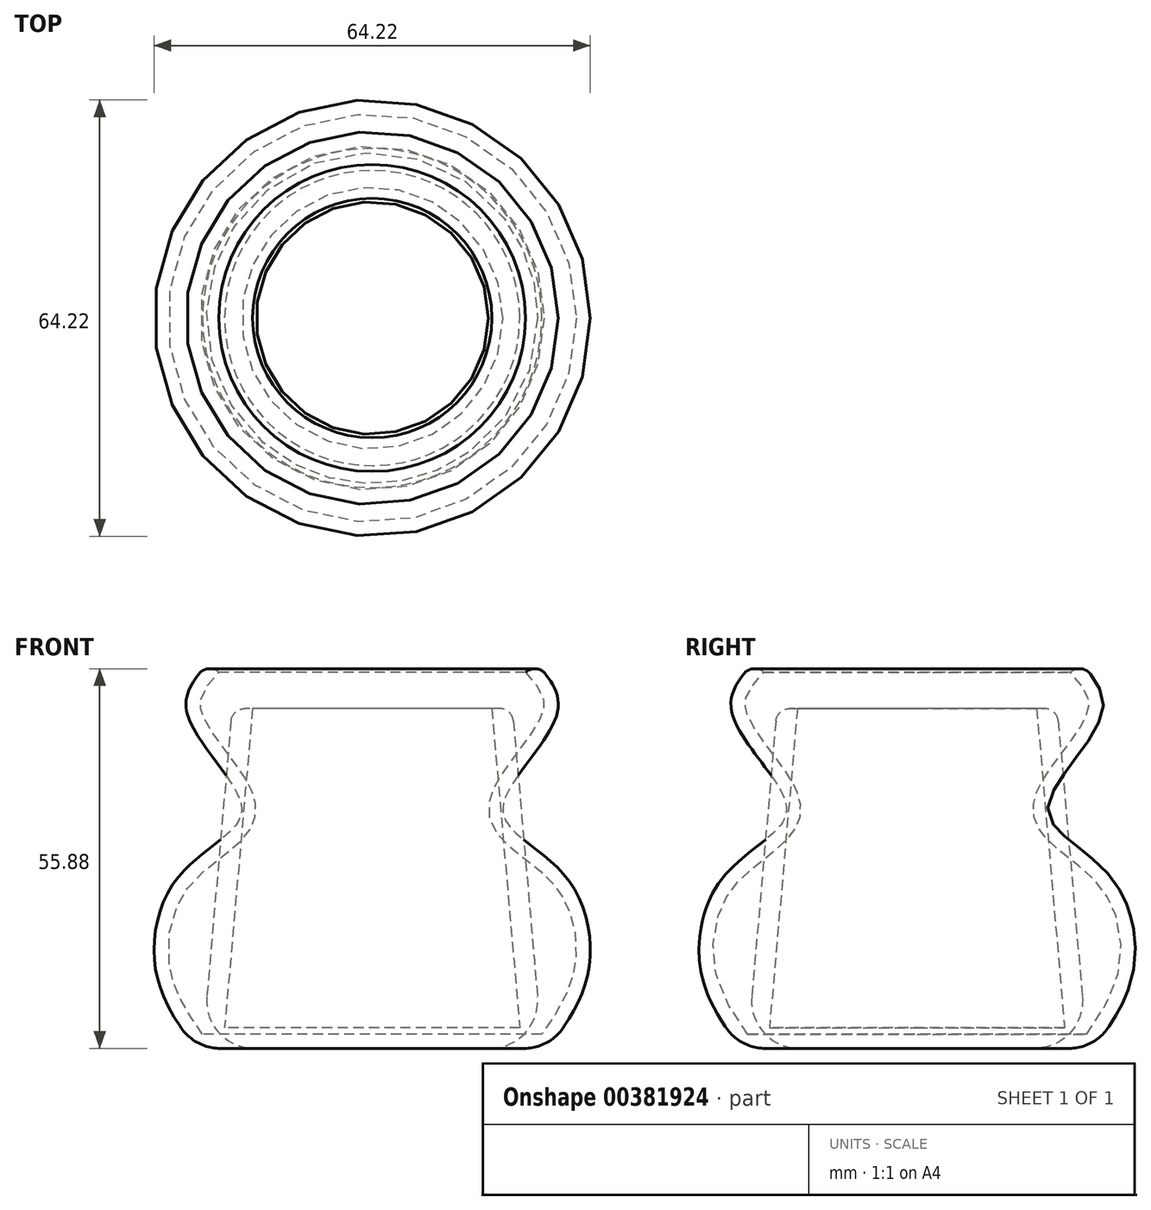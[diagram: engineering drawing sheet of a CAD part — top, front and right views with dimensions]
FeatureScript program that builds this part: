
annotation { "Feature Type Name" : "Feature", "Feature Type Description" : "" }
export const myFeature = defineFeature(function(context is Context, id is Id, definition is map)
    precondition{}
    {
        {
            var Q0;
            Q0=qCreatedBy(makeId("Top.planeOp"),FACE);
            var sketch = newSketch(context, id + "F0", { "sketchPlane" : qUnion([Q0])});
            skCircle(sketch, "E0", {"center": v(0, 0) * mm, "radius": 25 * mm});
            skSolve(sketch);
        }
        {
            var Q0;
            Q0=makeQuery(id+"F0.imprint","IMPRINT",FACE,{"disambiguationData":[TD([[makeQuery(id+"F0.imprint","IMPRINT",EDGE,{"derivedFrom":sQuery(id+"F0.wireOp",EDGE,"E0")}),1.0]])]});
            extrude(context, id + "F1", {"entities" : qUnion([Q0]), "depth" : 50 * mm, "hasDraft" : true, "draftAngle" : 5 * degree, "draftPullDirection" : true});
        }
        {
            var Q0;
            Q0=makeQuery(id+"F1.opExtrude","CAP_FACE",FACE,{"disambiguationData":[OSD([sQuery(id+"F0.wireOp",EDGE,"E0")])],"isStart":false});
            shell(context, id + "F2", {"entities" : qUnion([Q0]), "thickness" : 3 * mm});
        }
        {
            var Q0;
            Q0=makeQuery(id+"F1.opExtrude","CAP_EDGE",EDGE,{"disambiguationData":[OSD([sQuery(id+"F0.wireOp",EDGE,"E0")])],"isStart":false});
            fillet(context, id + "F3", {"entities" : qUnion([Q0]), "radius" : 2 * mm, "tangentPropagation" : true, "allowEdgeOverflow" : false});
        }
        {
            var Q0;
            Q0=makeQuery(id+"F1.opExtrude","CAP_EDGE",EDGE,{"disambiguationData":[OSD([sQuery(id+"F0.wireOp",EDGE,"E0")])],"isStart":true});
            fillet(context, id + "F4", {"entities" : qUnion([Q0]), "radius" : 7 * mm, "tangentPropagation" : true, "allowEdgeOverflow" : false});
        }
        {
            var Q0;
            Q0=qCreatedBy(makeId("Right.planeOp"),FACE);
            var sketch = newSketch(context, id + "F5", { "sketchPlane" : qUnion([Q0])});
            skLineSegment(sketch, "E1", {"start": v(0, 60) * mm, "end": v(0, 0) * mm});
            skLineSegment(sketch, "E2", {"start": v(26.06, 0) * mm, "end": v(0, 0) * mm});
            skFitSpline(sketch, "E3", {"points": [v(24.17, 56.72) * mm, v(27.28, 49.46) * mm, v(19.44, 36.48) * mm, v(21.4, 31.5) * mm, v(29.33, 24.16) * mm, v(31.8, 11.18) * mm, v(26.06, 0) * mm], "startDerivative": vector(39.21, -45.34) * mm, "endDerivative": vector(-40.58, -57.48) * mm});
            skLineSegment(sketch, "E4.1", {"start": v(24.97, 2.1) * mm, "end": v(2.1, 2.1) * mm});
            skFitSpline(sketch, "E4.2", {"points": [v(22.58, 55.35) * mm, v(22.99, 54.88) * mm, v(23.77, 53.97) * mm, v(24.68, 52.72) * mm, v(25.12, 51.79) * mm, v(25.29, 51.11) * mm, v(25.32, 50.7) * mm, v(25.3, 50.35) * mm, v(25.26, 50.07) * mm, v(25.2, 49.77) * mm, v(25.08, 49.42) * mm, v(24.94, 49.04) * mm, v(24.69, 48.5) * mm, v(24.13, 47.45) * mm, v(23.03, 45.77) * mm, v(21.45, 43.64) * mm, v(20.1, 41.84) * mm, v(19.11, 40.41) * mm, v(18.44, 39.34) * mm, v(17.96, 38.44) * mm, v(17.64, 37.7) * mm, v(17.43, 37.13) * mm, v(17.27, 36.54) * mm, v(17.14, 35.76) * mm, v(17.11, 34.79) * mm, v(17.32, 33.67) * mm, v(17.72, 32.67) * mm, v(18.26, 31.79) * mm, v(18.88, 31.02) * mm, v(19.55, 30.33) * mm, v(20.49, 29.48) * mm, v(21.74, 28.48) * mm, v(23.28, 27.29) * mm, v(24.8, 26.05) * mm, v(25.97, 24.96) * mm, v(26.8, 24.03) * mm, v(27.38, 23.3) * mm, v(27.89, 22.54) * mm, v(28.35, 21.7) * mm, v(28.76, 20.83) * mm, v(29.24, 19.6) * mm, v(29.7, 17.96) * mm, v(30, 15.91) * mm, v(30.04, 13.87) * mm, v(29.88, 12.22) * mm, v(29.62, 10.98) * mm, v(29.28, 9.75) * mm, v(28.71, 8.26) * mm, v(27.83, 6.5) * mm, v(26.43, 4.16) * mm, v(25.2, 2.4) * mm, v(24.35, 1.21) * mm]});
            skLineSegment(sketch, "E5", {"start": v(22.58, 55.35) * mm, "end": v(24.17, 56.72) * mm});
            skLineSegment(sketch, "E6", {"start": v(2.1, 2.1) * mm, "end": v(0, 2.1) * mm});
            skSolve(sketch);
        }
        {
            var Q0;
            {var subQ0=sQuery(id+"F5.wireOp",EDGE,"E2");Q0=makeQuery(id+"F5.imprint","IMPRINT",FACE,{"disambiguationData":[TD([[makeQuery(id+"F5.imprint","IMPRINT",EDGE,{"derivedFrom":subQ0}),-1.0]])]});}
            var Q1;
            Q1=sQuery(id+"F5.wireOp",EDGE,"E1");
            revolve(context, id + "F6", {"entities" : qUnion([Q0]), "axis" : qUnion([Q1]), "revolveType" : RevolveType.FULL});
        }
        {
            var Q0;
            Q0=makeQuery(id+"F6.opRevolve","SWEPT_EDGE",EDGE,{"disambiguationData":[OSD([sQuery(id+"F5.wireOp",EDGE,"E2"),sQuery(id+"F5.wireOp",EDGE,"E3")])]});
            fillet(context, id + "F7", {"entities" : qUnion([Q0]), "radius" : 7 * mm, "tangentPropagation" : true, "allowEdgeOverflow" : false});
        }
        {
            var Q0;
            Q0=makeQuery(id+"F6.opRevolve","SWEPT_EDGE",EDGE,{"disambiguationData":[OSD([sQuery(id+"F5.wireOp",EDGE,"E3"),sQuery(id+"F5.wireOp",EDGE,"E5")])]});
            fillet(context, id + "F8", {"entities" : qUnion([Q0]), "radius" : 2 * mm, "tangentPropagation" : true, "allowEdgeOverflow" : false});
        }
    });
